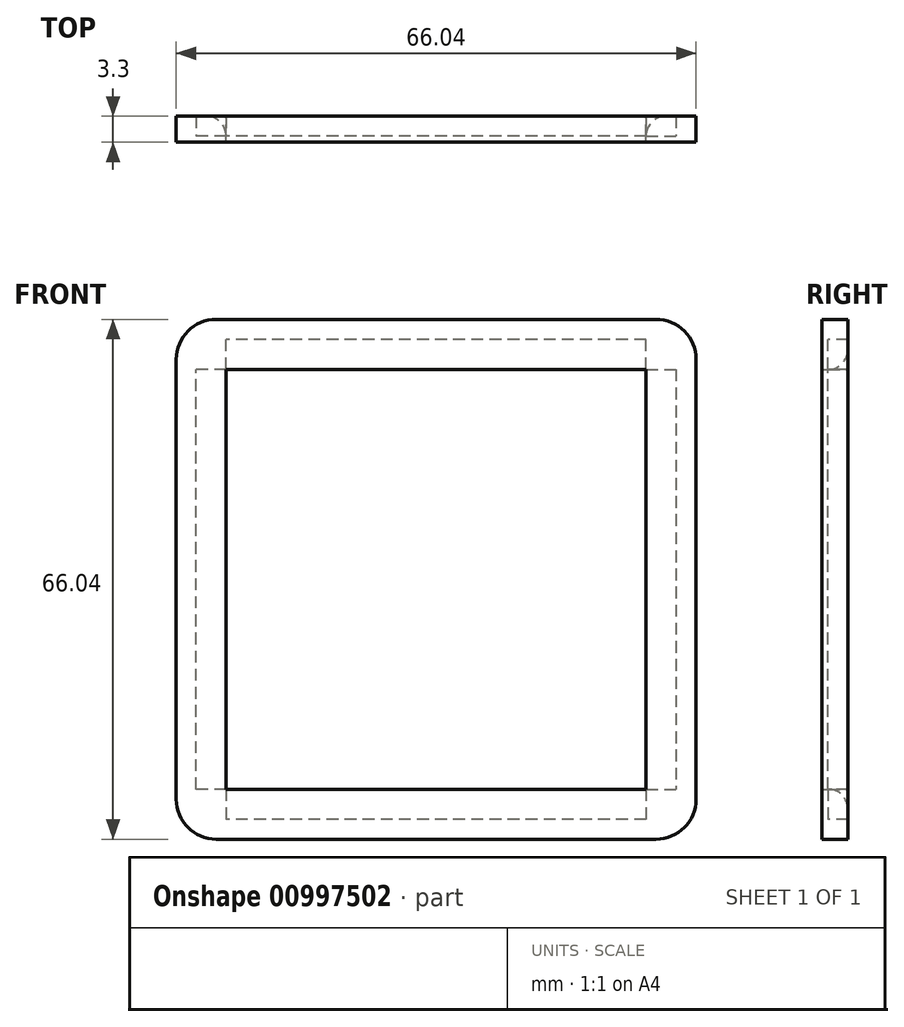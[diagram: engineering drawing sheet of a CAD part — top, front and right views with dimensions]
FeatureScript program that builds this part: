
annotation { "Feature Type Name" : "Feature", "Feature Type Description" : "" }
export const myFeature = defineFeature(function(context is Context, id is Id, definition is map)
    precondition{}
    {
        {
            var Q0;
            Q0=qCreatedBy(makeId("Front.planeOp"),FACE);
            var sketch = newSketch(context, id + "F0", { "sketchPlane" : qUnion([Q0])});
            skLineSegment(sketch, "E0.bottom", {"start": v(-373.07, -265.06) * mm, "end": v(-307.03, -265.06) * mm});
            skLineSegment(sketch, "E0.top", {"start": v(-373.07, -331.1) * mm, "end": v(-307.03, -331.1) * mm});
            skLineSegment(sketch, "E0.left", {"start": v(-373.07, -265.06) * mm, "end": v(-373.07, -331.1) * mm});
            skLineSegment(sketch, "E0.right", {"start": v(-307.03, -265.06) * mm, "end": v(-307.03, -331.1) * mm});
            skLineSegment(sketch, "E1.0", {"start": v(-366.72, -271.4) * mm, "end": v(-366.72, -324.75) * mm});
            skLineSegment(sketch, "E1.1", {"start": v(-366.72, -271.4) * mm, "end": v(-313.38, -271.4) * mm});
            skLineSegment(sketch, "E1.2", {"start": v(-313.38, -271.4) * mm, "end": v(-313.38, -324.75) * mm});
            skLineSegment(sketch, "E1.3", {"start": v(-366.72, -324.75) * mm, "end": v(-313.38, -324.75) * mm});
            skSolve(sketch);
        }
        {
            var Q0;
            Q0=makeQuery(id+"F0.imprint","IMPRINT",FACE,{"disambiguationData":[TD([[makeQuery(id+"F0.imprint","IMPRINT",EDGE,{"derivedFrom":sQuery(id+"F0.wireOp",EDGE,"E0.bottom")}),-1.0]])]});
            extrude(context, id + "F1", {"entities" : qUnion([Q0]), "depth" : 3.3 * mm, "offsetDistance" : 25.4 * mm});
        }
        {
            var Q0;
            Q0=makeQuery(id+"F1.opExtrude","SWEPT_EDGE",EDGE,{"disambiguationData":[OSD([sQuery(id+"F0.wireOp",EDGE,"E0.top"),sQuery(id+"F0.wireOp",EDGE,"E0.right")])]});
            var Q1;
            Q1=makeQuery(id+"F1.opExtrude","SWEPT_EDGE",EDGE,{"disambiguationData":[OSD([sQuery(id+"F0.wireOp",EDGE,"E0.top"),sQuery(id+"F0.wireOp",EDGE,"E0.left")])]});
            var Q2;
            Q2=makeQuery(id+"F1.opExtrude","SWEPT_EDGE",EDGE,{"disambiguationData":[OSD([sQuery(id+"F0.wireOp",EDGE,"E0.bottom"),sQuery(id+"F0.wireOp",EDGE,"E0.left")])]});
            var Q3;
            Q3=makeQuery(id+"F1.opExtrude","SWEPT_EDGE",EDGE,{"disambiguationData":[OSD([sQuery(id+"F0.wireOp",EDGE,"E0.bottom"),sQuery(id+"F0.wireOp",EDGE,"E0.right")])]});
            fillet(context, id + "F2", {"entities" : qUnion([Q0, Q1, Q2, Q3]), "radius" : 5.08 * mm, "tangentPropagation" : true, "allowEdgeOverflow" : false});
        }
        {
            var Q0;
            Q0=makeQuery(id+"F1.opExtrude","CAP_FACE",FACE,{"disambiguationData":[OSD([sQuery(id+"F0.wireOp",EDGE,"E0.bottom"),sQuery(id+"F0.wireOp",EDGE,"E0.top"),sQuery(id+"F0.wireOp",EDGE,"E0.left"),sQuery(id+"F0.wireOp",EDGE,"E0.right"),sQuery(id+"F0.wireOp",EDGE,"E1.0"),sQuery(id+"F0.wireOp",EDGE,"E1.1"),sQuery(id+"F0.wireOp",EDGE,"E1.2"),sQuery(id+"F0.wireOp",EDGE,"E1.3")])],"isStart":true});
            var sketch = newSketch(context, id + "F3", { "sketchPlane" : qUnion([Q0])});
            skLineSegment(sketch, "E2.bottom", {"start": v(313.38, -271.4) * mm, "end": v(366.72, -271.4) * mm});
            skLineSegment(sketch, "E2.top", {"start": v(313.38, -267.6) * mm, "end": v(366.72, -267.6) * mm});
            skLineSegment(sketch, "E2.left", {"start": v(313.38, -271.4) * mm, "end": v(313.38, -267.6) * mm});
            skLineSegment(sketch, "E2.right", {"start": v(366.72, -271.4) * mm, "end": v(366.72, -267.6) * mm});
            skLineSegment(sketch, "E3.bottom", {"start": v(313.38, -271.4) * mm, "end": v(309.57, -271.4) * mm});
            skLineSegment(sketch, "E3.top", {"start": v(313.38, -324.75) * mm, "end": v(309.57, -324.75) * mm});
            skLineSegment(sketch, "E3.left", {"start": v(313.38, -271.4) * mm, "end": v(313.38, -324.75) * mm});
            skLineSegment(sketch, "E3.right", {"start": v(309.57, -271.4) * mm, "end": v(309.57, -324.75) * mm});
            skLineSegment(sketch, "E4.bottom", {"start": v(313.38, -324.75) * mm, "end": v(366.72, -324.75) * mm});
            skLineSegment(sketch, "E4.top", {"start": v(313.38, -328.56) * mm, "end": v(366.72, -328.56) * mm});
            skLineSegment(sketch, "E4.left", {"start": v(313.38, -324.75) * mm, "end": v(313.38, -328.56) * mm});
            skLineSegment(sketch, "E4.right", {"start": v(366.72, -324.75) * mm, "end": v(366.72, -328.56) * mm});
            skLineSegment(sketch, "E5.bottom", {"start": v(366.72, -324.75) * mm, "end": v(370.53, -324.75) * mm});
            skLineSegment(sketch, "E5.top", {"start": v(366.72, -271.4) * mm, "end": v(370.53, -271.4) * mm});
            skLineSegment(sketch, "E5.left", {"start": v(366.72, -324.75) * mm, "end": v(366.72, -271.4) * mm});
            skLineSegment(sketch, "E5.right", {"start": v(370.53, -324.75) * mm, "end": v(370.53, -271.4) * mm});
            skPoint(sketch, "E6", {"position": v(366.72, -271.4) * mm});
            skPoint(sketch, "E7", {"position": v(370.53, -271.4) * mm});
            skPoint(sketch, "E8", {"position": v(366.72, -267.6) * mm});
            skPoint(sketch, "E9", {"position": v(313.38, -271.4) * mm});
            skPoint(sketch, "E10", {"position": v(309.57, -271.4) * mm});
            skPoint(sketch, "E11", {"position": v(313.38, -267.6) * mm});
            skPoint(sketch, "E12", {"position": v(313.38, -324.75) * mm});
            skPoint(sketch, "E13", {"position": v(309.57, -324.75) * mm});
            skPoint(sketch, "E14", {"position": v(313.38, -328.56) * mm});
            skPoint(sketch, "E15", {"position": v(366.72, -328.56) * mm});
            skPoint(sketch, "E16", {"position": v(366.72, -324.75) * mm});
            skPoint(sketch, "E17", {"position": v(370.53, -324.75) * mm});
            skSolve(sketch);
        }
        {
            var Q0;
            Q0=makeQuery(id+"F3.imprint","IMPRINT",FACE,{"disambiguationData":[TD([[makeQuery(id+"F3.imprint","IMPRINT",EDGE,{"derivedFrom":sQuery(id+"F3.wireOp",EDGE,"E4.bottom")}),1.0]])]});
            var Q1;
            Q1=makeQuery(id+"F3.imprint","IMPRINT",FACE,{"disambiguationData":[TD([[makeQuery(id+"F3.imprint","IMPRINT",EDGE,{"derivedFrom":sQuery(id+"F3.wireOp",EDGE,"E5.bottom")}),1.0]])]});
            var Q2;
            Q2=makeQuery(id+"F3.imprint","IMPRINT",FACE,{"disambiguationData":[TD([[makeQuery(id+"F3.imprint","IMPRINT",EDGE,{"derivedFrom":sQuery(id+"F3.wireOp",EDGE,"E2.bottom")}),-1.0]])]});
            var Q3;
            Q3=makeQuery(id+"F3.imprint","IMPRINT",FACE,{"disambiguationData":[TD([[makeQuery(id+"F3.imprint","IMPRINT",EDGE,{"derivedFrom":sQuery(id+"F3.wireOp",EDGE,"E3.bottom")}),1.0]])]});
            extrude(context, id + "F4", {"entities" : qUnion([Q0, Q1, Q2, Q3]), "operationType" : NewBodyOperationType.REMOVE, "oppositeDirection" : true, "depth" : 2.54 * mm, "offsetDistance" : 25.4 * mm});
        }
        {
            var Q0;
            Q0=makeQuery(id+"F4.boolean.opBoolean","COPY",FACE,{"derivedFrom":makeQuery(id+"F4.opExtrude","CAP_FACE",FACE,{"disambiguationData":[OSD([sQuery(id+"F3.wireOp",EDGE,"E3.bottom"),sQuery(id+"F3.wireOp",EDGE,"E3.top"),sQuery(id+"F3.wireOp",EDGE,"E3.left"),sQuery(id+"F3.wireOp",EDGE,"E3.right")])],"isStart":false})});
            var sketch = newSketch(context, id + "F5", { "sketchPlane" : qUnion([Q0])});
            skLineSegment(sketch, "E18.bottom", {"start": v(309.57, -271.4) * mm, "end": v(313.38, -271.4) * mm});
            skLineSegment(sketch, "E18.top", {"start": v(309.57, -324.75) * mm, "end": v(313.38, -324.75) * mm});
            skLineSegment(sketch, "E18.left", {"start": v(309.57, -271.4) * mm, "end": v(309.57, -324.75) * mm});
            skLineSegment(sketch, "E18.right", {"start": v(313.38, -271.4) * mm, "end": v(313.38, -324.75) * mm});
            skSolve(sketch);
        }
        {
            var Q0;
            Q0=makeQuery(id+"F4.boolean.opBoolean","COPY",FACE,{"derivedFrom":makeQuery(id+"F4.opExtrude","CAP_FACE",FACE,{"disambiguationData":[OSD([sQuery(id+"F3.wireOp",EDGE,"E4.bottom"),sQuery(id+"F3.wireOp",EDGE,"E4.top"),sQuery(id+"F3.wireOp",EDGE,"E4.left"),sQuery(id+"F3.wireOp",EDGE,"E4.right")])],"isStart":false})});
            var sketch = newSketch(context, id + "F6", { "sketchPlane" : qUnion([Q0])});
            skLineSegment(sketch, "E19.bottom", {"start": v(313.38, -328.56) * mm, "end": v(366.72, -328.56) * mm});
            skLineSegment(sketch, "E19.top", {"start": v(313.38, -324.75) * mm, "end": v(366.72, -324.75) * mm});
            skLineSegment(sketch, "E19.left", {"start": v(313.38, -328.56) * mm, "end": v(313.38, -324.75) * mm});
            skLineSegment(sketch, "E19.right", {"start": v(366.72, -328.56) * mm, "end": v(366.72, -324.75) * mm});
            skSolve(sketch);
        }
        {
            var Q0;
            Q0=makeQuery(id+"F4.boolean.opBoolean","COPY",FACE,{"derivedFrom":makeQuery(id+"F4.opExtrude","CAP_FACE",FACE,{"disambiguationData":[OSD([sQuery(id+"F3.wireOp",EDGE,"E5.bottom"),sQuery(id+"F3.wireOp",EDGE,"E5.top"),sQuery(id+"F3.wireOp",EDGE,"E5.left"),sQuery(id+"F3.wireOp",EDGE,"E5.right")])],"isStart":false})});
            var sketch = newSketch(context, id + "F7", { "sketchPlane" : qUnion([Q0])});
            skLineSegment(sketch, "E20.bottom", {"start": v(366.72, -324.75) * mm, "end": v(370.53, -324.75) * mm});
            skLineSegment(sketch, "E20.top", {"start": v(366.72, -271.4) * mm, "end": v(370.53, -271.4) * mm});
            skLineSegment(sketch, "E20.left", {"start": v(366.72, -324.75) * mm, "end": v(366.72, -271.4) * mm});
            skLineSegment(sketch, "E20.right", {"start": v(370.53, -324.75) * mm, "end": v(370.53, -271.4) * mm});
            skSolve(sketch);
        }
        {
            var Q0;
            Q0=makeQuery(id+"F4.boolean.opBoolean","COPY",FACE,{"derivedFrom":makeQuery(id+"F4.opExtrude","CAP_FACE",FACE,{"disambiguationData":[OSD([sQuery(id+"F3.wireOp",EDGE,"E2.bottom"),sQuery(id+"F3.wireOp",EDGE,"E2.top"),sQuery(id+"F3.wireOp",EDGE,"E2.left"),sQuery(id+"F3.wireOp",EDGE,"E2.right")])],"isStart":false})});
            var sketch = newSketch(context, id + "F8", { "sketchPlane" : qUnion([Q0])});
            skLineSegment(sketch, "E21.bottom", {"start": v(313.38, -267.6) * mm, "end": v(366.72, -267.6) * mm});
            skLineSegment(sketch, "E21.top", {"start": v(313.38, -271.4) * mm, "end": v(366.72, -271.4) * mm});
            skLineSegment(sketch, "E21.left", {"start": v(313.38, -267.6) * mm, "end": v(313.38, -271.4) * mm});
            skLineSegment(sketch, "E21.right", {"start": v(366.72, -267.6) * mm, "end": v(366.72, -271.4) * mm});
            skSolve(sketch);
        }
        {
            var Q0;
            Q0=makeQuery(id+"F6.imprint","IMPRINT",FACE,{"disambiguationData":[TD([[makeQuery(id+"F6.imprint","IMPRINT",EDGE,{"derivedFrom":sQuery(id+"F6.wireOp",EDGE,"E19.bottom")}),1.0]])]});
            var Q1;
            Q1=makeQuery(id+"F5.imprint","IMPRINT",FACE,{"disambiguationData":[TD([[makeQuery(id+"F5.imprint","IMPRINT",EDGE,{"derivedFrom":sQuery(id+"F5.wireOp",EDGE,"E18.bottom")}),1.0]])]});
            var Q2;
            Q2=makeQuery(id+"F8.imprint","IMPRINT",FACE,{"disambiguationData":[TD([[makeQuery(id+"F8.imprint","IMPRINT",EDGE,{"derivedFrom":sQuery(id+"F8.wireOp",EDGE,"E21.bottom")}),-1.0]])]});
            var Q3;
            Q3=makeQuery(id+"F7.imprint","IMPRINT",FACE,{"disambiguationData":[TD([[makeQuery(id+"F7.imprint","IMPRINT",EDGE,{"derivedFrom":sQuery(id+"F7.wireOp",EDGE,"E20.bottom")}),1.0]])]});
            extrude(context, id + "F9", {"entities" : qUnion([Q0, Q1, Q2, Q3]), "depth" : 2.54 * mm, "offsetDistance" : 25.4 * mm});
        }
        {
            var Q0;
            Q0=makeQuery(id+"F9.opExtrude","CAP_EDGE",EDGE,{"disambiguationData":[OSD([sQuery(id+"F5.wireOp",EDGE,"E18.right")])],"isStart":false});
            var Q1;
            Q1=makeQuery(id+"F9.opExtrude","CAP_EDGE",EDGE,{"disambiguationData":[OSD([sQuery(id+"F6.wireOp",EDGE,"E19.top")])],"isStart":false});
            var Q2;
            Q2=makeQuery(id+"F9.opExtrude","CAP_EDGE",EDGE,{"disambiguationData":[OSD([sQuery(id+"F7.wireOp",EDGE,"E20.left")])],"isStart":false});
            var Q3;
            Q3=makeQuery(id+"F9.opExtrude","CAP_EDGE",EDGE,{"disambiguationData":[OSD([sQuery(id+"F8.wireOp",EDGE,"E21.top")])],"isStart":false});
            fillet(context, id + "F10", {"entities" : qUnion([Q0, Q1, Q2, Q3]), "radius" : 2.54 * mm, "tangentPropagation" : true, "allowEdgeOverflow" : false});
        }
    });
